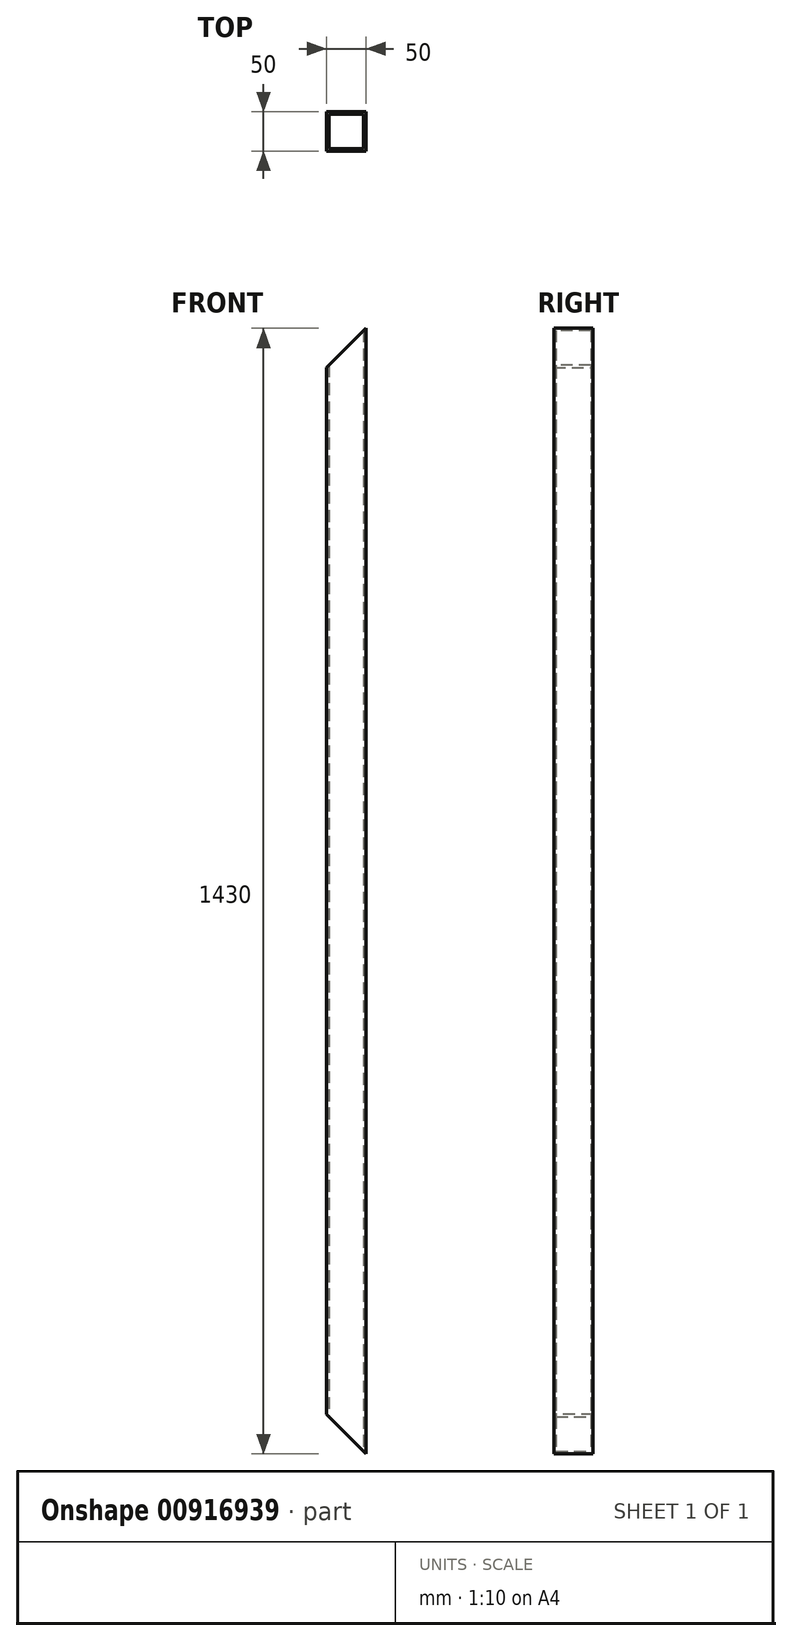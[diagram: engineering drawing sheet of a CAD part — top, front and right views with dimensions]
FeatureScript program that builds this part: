
annotation { "Feature Type Name" : "Feature", "Feature Type Description" : "" }
export const myFeature = defineFeature(function(context is Context, id is Id, definition is map)
    precondition{}
    {
        {
            var Q0;
            Q0=qCreatedBy(makeId("Top.planeOp"),FACE);
            var sketch = newSketch(context, id + "F0", { "sketchPlane" : qUnion([Q0])});
            skLineSegment(sketch, "E0.bottom", {"start": v(0, 0) * mm, "end": v(50, 0) * mm});
            skLineSegment(sketch, "E0.top", {"start": v(0, 50) * mm, "end": v(50, 50) * mm});
            skLineSegment(sketch, "E0.left", {"start": v(0, 0) * mm, "end": v(0, 50) * mm});
            skLineSegment(sketch, "E0.right", {"start": v(50, 0) * mm, "end": v(50, 50) * mm});
            skLineSegment(sketch, "E1.0", {"start": v(3, 3) * mm, "end": v(47, 3) * mm});
            skLineSegment(sketch, "E1.1", {"start": v(3, 3) * mm, "end": v(3, 47) * mm});
            skLineSegment(sketch, "E1.2", {"start": v(3, 47) * mm, "end": v(47, 47) * mm});
            skLineSegment(sketch, "E1.3", {"start": v(47, 3) * mm, "end": v(47, 47) * mm});
            skSolve(sketch);
        }
        {
            var Q0;
            Q0=makeQuery(id+"F0.imprint","IMPRINT",FACE,{"disambiguationData":[TD([[makeQuery(id+"F0.imprint","IMPRINT",EDGE,{"derivedFrom":sQuery(id+"F0.wireOp",EDGE,"E0.bottom")}),1.0]])]});
            extrude(context, id + "F1", {"entities" : qUnion([Q0]), "depth" : 1430 * mm, "offsetDistance" : 25 * mm});
        }
        {
            var Q0;
            Q0=makeQuery(id+"F1.opExtrude","CAP_EDGE",EDGE,{"disambiguationData":[OSD([sQuery(id+"F0.wireOp",EDGE,"E0.left")])],"isStart":true});
            var Q1;
            Q1=makeQuery(id+"F1.opExtrude","CAP_EDGE",EDGE,{"disambiguationData":[OSD([sQuery(id+"F0.wireOp",EDGE,"E0.left")])],"isStart":false});
            chamfer(context, id + "F2", {"entities" : qUnion([Q0, Q1]), "width" : 50 * mm, "tangentPropagation" : true});
        }
    });
